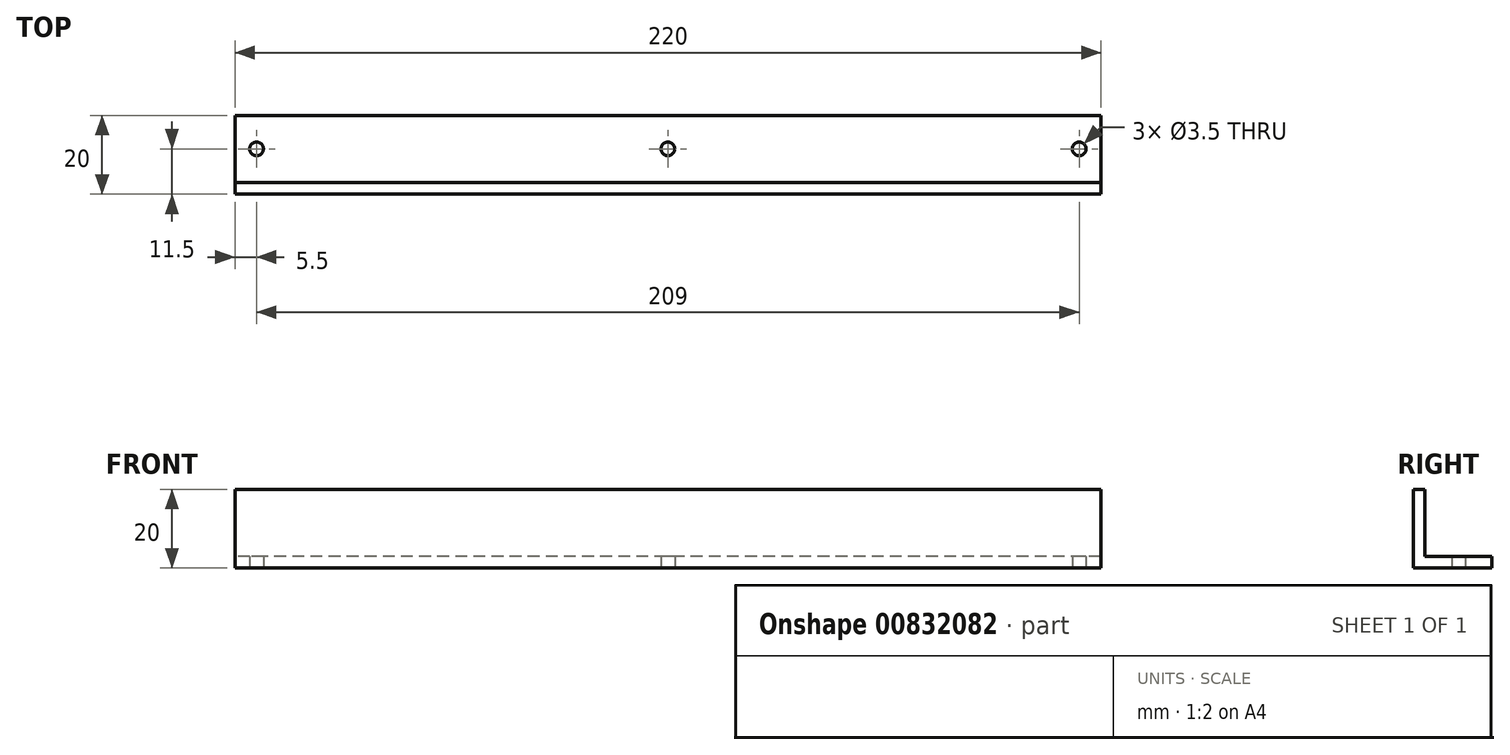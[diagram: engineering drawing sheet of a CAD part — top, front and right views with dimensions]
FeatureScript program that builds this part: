
annotation { "Feature Type Name" : "Feature", "Feature Type Description" : "" }
export const myFeature = defineFeature(function(context is Context, id is Id, definition is map)
    precondition{}
    {
        {
            var Q0;
            Q0=qCreatedBy(makeId("Right.planeOp"),FACE);
            var sketch = newSketch(context, id + "F0", { "sketchPlane" : qUnion([Q0])});
            skLineSegment(sketch, "E0", {"start": v(0, 0) * mm, "end": v(0, 20) * mm});
            skLineSegment(sketch, "E1", {"start": v(0, 20) * mm, "end": v(3, 20) * mm});
            skLineSegment(sketch, "E2", {"start": v(3, 20) * mm, "end": v(3, 3) * mm});
            skLineSegment(sketch, "E3", {"start": v(3, 3) * mm, "end": v(20, 3) * mm});
            skLineSegment(sketch, "E4", {"start": v(20, 3) * mm, "end": v(20, 0) * mm});
            skLineSegment(sketch, "E5", {"start": v(20, 0) * mm, "end": v(0, 0) * mm});
            skSolve(sketch);
        }
        {
            var Q0;
            Q0 = qSketchRegion(id + "F0", true);
            extrude(context, id + "F1", {"entities" : qUnion([Q0]), "depth" : 220 * mm, "offsetDistance" : 25 * mm});
        }
        {
            var Q0;
            Q0=makeQuery(id+"F1.opExtrude","SWEPT_FACE",FACE,{"disambiguationData":[OSD([sQuery(id+"F0.wireOp",EDGE,"E5")])]});
            var sketch = newSketch(context, id + "F2", { "sketchPlane" : qUnion([Q0])});
            skLineSegment(sketch, "E6", {"start": v(0, -11.5) * mm, "end": v(220, -11.5) * mm, "construction": true});
            skCircle(sketch, "E7", {"center": v(110, -11.5) * mm, "radius": 1.75 * mm});
            skCircle(sketch, "E8", {"center": v(5.5, -11.5) * mm, "radius": 1.75 * mm});
            skCircle(sketch, "E9", {"center": v(214.5, -11.5) * mm, "radius": 1.75 * mm});
            skPoint(sketch, "E10.0", {"position": v(0, -20) * mm});
            skPoint(sketch, "E11.0", {"position": v(220, -20) * mm});
            skSolve(sketch);
        }
        {
            var Q0;
            Q0=makeQuery(id+"F2.imprint","IMPRINT",FACE,{"disambiguationData":[TD([[makeQuery(id+"F2.imprint","IMPRINT",EDGE,{"derivedFrom":sQuery(id+"F2.wireOp",EDGE,"E8")}),1.0]])]});
            var Q1;
            Q1=makeQuery(id+"F2.imprint","IMPRINT",FACE,{"disambiguationData":[TD([[makeQuery(id+"F2.imprint","IMPRINT",EDGE,{"derivedFrom":sQuery(id+"F2.wireOp",EDGE,"E7")}),1.0]])]});
            var Q2;
            Q2=makeQuery(id+"F2.imprint","IMPRINT",FACE,{"disambiguationData":[TD([[makeQuery(id+"F2.imprint","IMPRINT",EDGE,{"derivedFrom":sQuery(id+"F2.wireOp",EDGE,"E9")}),1.0]])]});
            extrude(context, id + "F3", {"entities" : qUnion([Q0, Q1, Q2]), "operationType" : NewBodyOperationType.REMOVE, "oppositeDirection" : true, "depth" : 25 * mm, "offsetDistance" : 25 * mm});
        }
    });
